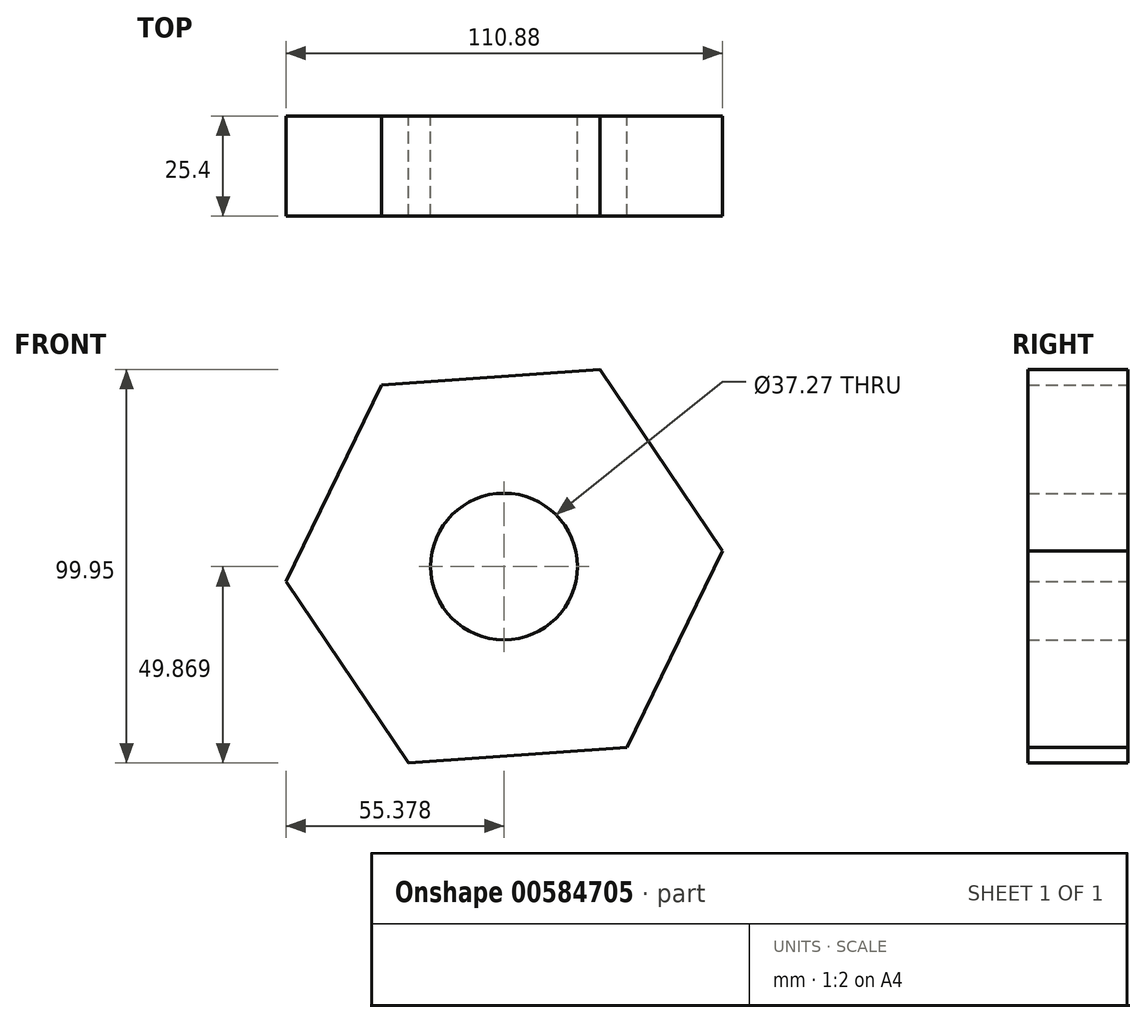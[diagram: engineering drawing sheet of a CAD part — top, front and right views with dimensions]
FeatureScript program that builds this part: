
annotation { "Feature Type Name" : "Feature", "Feature Type Description" : "" }
export const myFeature = defineFeature(function(context is Context, id is Id, definition is map)
    precondition{}
    {
        {
            var Q0;
            Q0=qCreatedBy(makeId("Front.planeOp"),FACE);
            var sketch = newSketch(context, id + "F0", { "sketchPlane" : qUnion([Q0])});
            skCircle(sketch, "E0.cCircle", {"center": v(-34.48, 44.38) * mm, "radius": 55.58 * mm, "construction": true});
            skLineSegment(sketch, "E0.0", {"start": v(20.96, 48.3) * mm, "end": v(-3.36, -1.67) * mm});
            skLineSegment(sketch, "E0.1", {"start": v(-3.36, -1.67) * mm, "end": v(-58.8, -5.6) * mm});
            skLineSegment(sketch, "E0.2", {"start": v(-58.8, -5.6) * mm, "end": v(-89.92, 40.45) * mm});
            skLineSegment(sketch, "E0.3", {"start": v(-89.92, 40.45) * mm, "end": v(-65.6, 90.43) * mm});
            skLineSegment(sketch, "E0.4", {"start": v(-65.6, 90.43) * mm, "end": v(-10.16, 94.35) * mm});
            skLineSegment(sketch, "E0.5", {"start": v(-10.16, 94.35) * mm, "end": v(20.96, 48.3) * mm});
            skSolve(sketch);
        }
        {
            var Q0;
            Q0=makeQuery(id+"F0.imprint","IMPRINT",FACE,{"disambiguationData":[TD([[makeQuery(id+"F0.imprint","IMPRINT",EDGE,{"derivedFrom":sQuery(id+"F0.wireOp",EDGE,"E0.0")}),-1.0]])]});
            var sketch = newSketch(context, id + "F1", { "sketchPlane" : qUnion([Q0])});
            skCircle(sketch, "E1", {"center": v(-34.54, 44.27) * mm, "radius": 18.64 * mm});
            skSolve(sketch);
        }
        {
            var Q0;
            Q0=makeQuery(id+"F1.imprint","IMPRINT",FACE,{"disambiguationData":[TD([[makeQuery(id+"F1.imprint","IMPRINT",EDGE,{"derivedFrom":sQuery(id+"F1.wireOp",EDGE,"E1")}),-1.0]])]});
            extrude(context, id + "F2", {"entities" : qUnion([Q0]), "depth" : 25.4 * mm, "offsetDistance" : 25.4 * mm});
        }
    });
